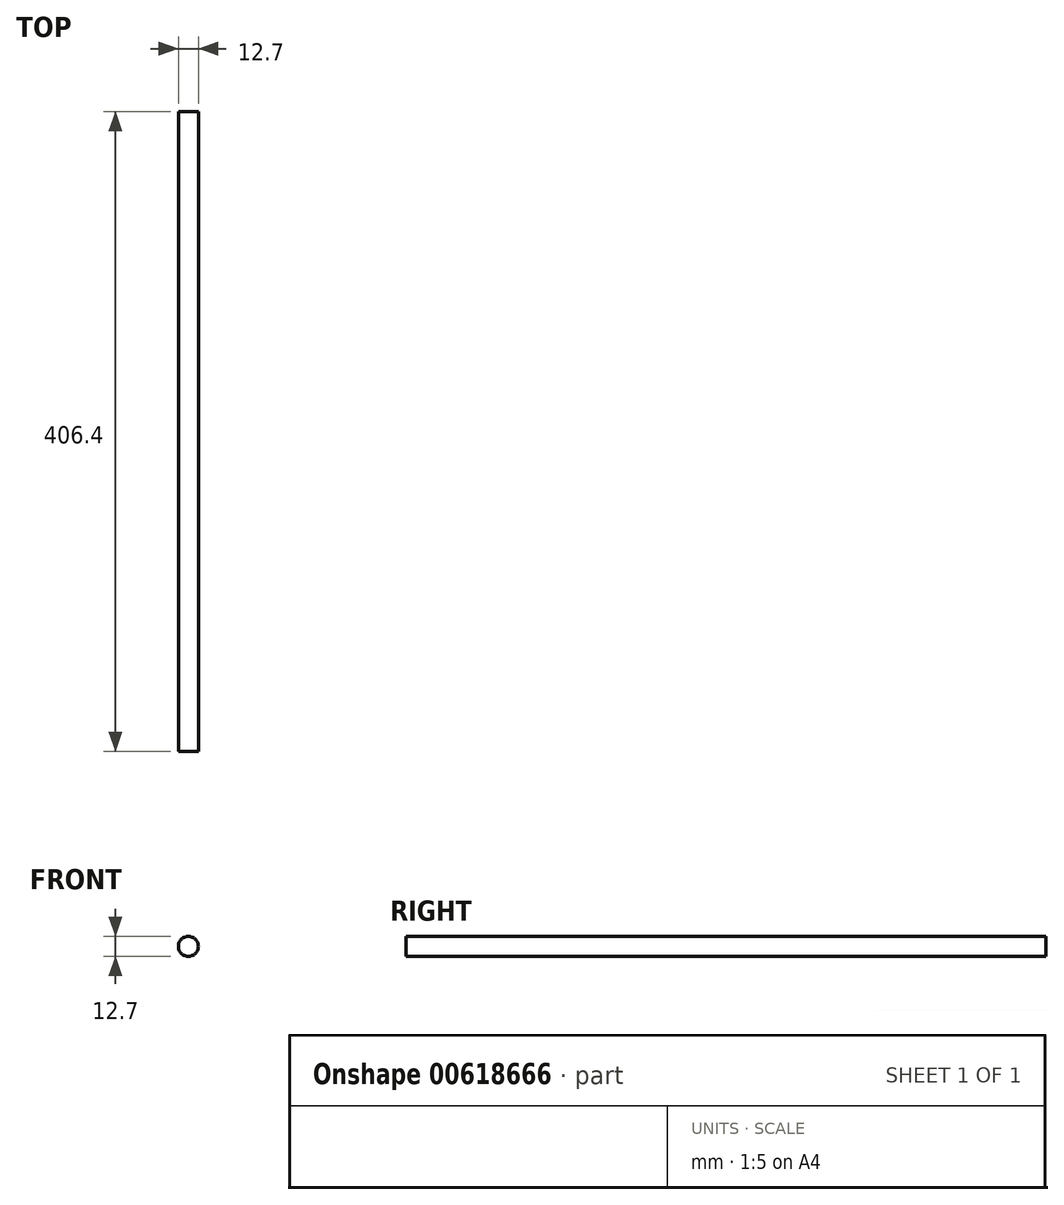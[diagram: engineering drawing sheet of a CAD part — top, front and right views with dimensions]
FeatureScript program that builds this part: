
annotation { "Feature Type Name" : "Feature", "Feature Type Description" : "" }
export const myFeature = defineFeature(function(context is Context, id is Id, definition is map)
    precondition{}
    {
        {
            var Q0;
            Q0=qCreatedBy(makeId("Front.planeOp"),FACE);
            var sketch = newSketch(context, id + "F0", { "sketchPlane" : qUnion([Q0])});
            skCircle(sketch, "E0", {"center": v(0, 0) * mm, "radius": 6.35 * mm});
            skSolve(sketch);
        }
        {
            var Q0;
            Q0=makeQuery(id+"F0.imprint","IMPRINT",FACE,{"disambiguationData":[TD([[makeQuery(id+"F0.imprint","IMPRINT",EDGE,{"derivedFrom":sQuery(id+"F0.wireOp",EDGE,"E0")}),1.0]])]});
            extrude(context, id + "F1", {"entities" : qUnion([Q0]), "depth" : 406.4 * mm, "offsetDistance" : 25.4 * mm});
        }
    });
